# Revit family: F1S_2903-2943-2606_OS275
name_source: partatom
category: Finestre
units: mm (PartAtom-declared; Revit-internal decimal feet)

## family parameters
Condiviso = No
Host = Muro
Numero OmniClass = 23.30.20.00
Punto di calcolo locali = Sì
Sempre verticale = Sì
Taglio con vuoti quando caricato = No
Titolo OmniClass = Windows

## types (4) — shared parameters
Altezza = 1500 mm  [stored 4.92126 ft]
Altezza di default del davanzale = 800 mm
Chiusura muro = Per host
Costruzione analitica = <Nessuno>
Descrizione = Finestra apertura a sporgere
H = 1500 mm  [stored 4.92126 ft]
H1 = 1500 mm  [stored 4.92126 ft]
H_Max = 1800 mm
H_Min = 800 mm
H_vetro = 1424 mm  [stored 4.67192 ft]
L = 900 mm  [stored 2.95276 ft]
L1 = 900 mm  [stored 2.95276 ft]
L_Max = 900 mm  [stored 2.95276 ft]
L_Min = 400 mm  [stored 1.31234 ft]
L_vetro = 824 mm  [stored 2.70341 ft]
Modello = OS2 75
Produttore = Secco Sistemi Spa
URL = https://www.seccosistemi.com

## per-type parameters (varying)
| type | Larghezza | MATERIALE | WARNING |
| Acciaio zincato | 1500 mm  [stored 4.92126 ft] | Acciaio | Sì |
| Acciaio inox | 1500 mm  [stored 4.92126 ft] | Acciaio inox, spazzolato | Sì |
| Acciaio corten | 1500 mm  [stored 4.92126 ft] | Acciaio corten | Sì |
| Ottone | 900 mm  [stored 2.95276 ft] | Ottone | No |

note: [stored X ft] marks values corroborated as IEEE doubles in the binary element streams (Revit-internal decimal feet)
